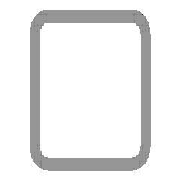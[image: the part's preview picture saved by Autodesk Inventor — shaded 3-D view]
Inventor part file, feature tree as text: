
AUTODESK INVENTOR PART (.ipt)
format: ipt  version: 2022 (Build 260153000, 153)  size: 139,264 bytes
history: native  units: mm (DEFAULTED — no unit token found)
features: other x4, plane x3, sketch x3, split x2
ambient origin geometry x8: Origin, YZ Plane, XZ Plane, XY Plane, X Axis, Y Axis, Z Axis, Center Point
bodies: Solid1 (feature_tree), Body (feature_tree)
feature tree (12):
  parser-record x1  (decoder bookkeeping rows leaked as tree rows — omitted from the tree; the rows remain in map.json)
  other  "Driven Length"
  other  "Start Plane"
  other  "End Plane"
  plane  "Work Plane4"
  split  "Split1"
  plane  "Work Plane5"
  split  "Split2"
  sketch  "Sketch"  dims[d7=8.0mm d9=40.0mm d11=40.0mm d12=4.0mm d13=20.0mm d14=160.0mm d15=20.0mm d16=20.0mm d17=90.0deg d18=140.0mm]
  sketch  "Sketch3"  dims[d3=140.0mm]
  plane  "Work Plane3"
  sketch  "Sketch4"  dims[d4=0.0mm]
